# Revit family: Cadet
name_source: partatom
category: Lighting Fixtures
revit_build: Autodesk Revit Architecture 2012 (Build: 20110309_2315(x64)
units: mm (PartAtom-declared; Revit-internal decimal feet)

## types (12) — shared parameters
Apparent Load = 0 VA
Default Elevation = 48 "
Description = Cadet LED Floodlight
Glass = Hubbell - Glass
Lamp = LED
Manufacturer = Hubbell Outdoor Lighting
Manufacturer Fax = 941-751-5535
Model = Cadet
Pivot Angle = 45.00°
Visor Option = CDT : HV
Voltage = 120-277V
zz Angle 1 = 45.00°

## per-type parameters (varying)
| type | Photometric Web | Product Documentation Link | Product Material | Product Page URL | URL | Watt |
| Basic Black Textured | Web : CDT-24NB-55-3K-2X2 | http://www.beaconproducts.com | Paint - Hubbell - Basic Black Textured | http://www.beaconproducts.com | http://www.beaconproducts.com | 55 W |
| Gray Smooth | Web : CDT-24NB-55-3K-2X2 | http://www.hubbelloutdoor.com | Paint - Hubbell - Gray Smooth | http://www.hubbelloutdoor.com | http://www.hubbelloutdoor.com | 30 W |
| Black Matte Textured | Web : CDT-24NB-55-3K-2X2 | http://www.hubbelloutdoor.com | Paint - Hubbell - Black Matte Textured | http://www.hubbelloutdoor.com | http://www.hubbelloutdoor.com | 30 W |
| Bronze Textured | Web : CDT-24NB-55-3K-2X2 | http://www.hubbelloutdoor.com | Paint - Hubbell - Bronze Textured | http://www.hubbelloutdoor.com | http://www.hubbelloutdoor.com | 30 W |
| Dark Bronze Textured | Web : CDT-24NB-55-3K-2X2 | http://www.hubbelloutdoor.com | Paint - Hubbell - Dark Bronze Textured | http://www.hubbelloutdoor.com | http://www.hubbelloutdoor.com | 30 W |
| Dark Platinum Smooth | Web : CDT-24NB-55-3K-2X2 | http://www.hubbelloutdoor.com | Paint - Hubbell - Dark Platinum Smooth | http://www.hubbelloutdoor.com | http://www.hubbelloutdoor.com | 30 W |
| Green Textured | Web : CDT-24NB-55-3K-2X2 | http://www.hubbelloutdoor.com | Paint - Hubbell - Green Textured | http://www.hubbelloutdoor.com | http://www.hubbelloutdoor.com | 30 W |
| Metallic Bronze Textured | Web : CDT-24NB-55-3K-2X2 | http://www.hubbelloutdoor.com | Paint - Hubbell - Metallic Bronze Textured | http://www.hubbelloutdoor.com | http://www.hubbelloutdoor.com | 30 W |
| Metallic Silver Textured | Web : CDT-24NB-55-4K-5X5 | http://www.hubbelloutdoor.com | Paint - Hubbell - Metallic Silver Textured | http://www.hubbelloutdoor.com | http://www.hubbelloutdoor.com | 30 W |
| Metallic Titanium Textured | Web : CDT-24NB-55-3K-2X2 | http://www.hubbelloutdoor.com | Paint - Hubbell - Metallic Titanium Textured | http://www.hubbelloutdoor.com | http://www.hubbelloutdoor.com | 30 W |
| Old World Iron | Web : CDT-24NB-55-3K-2X2 | http://www.hubbelloutdoor.com | Paint - Hubbell - Old World Iron | http://www.hubbelloutdoor.com | http://www.hubbelloutdoor.com | 30 W |
| White Texture | Web : CDT-24NB-55-3K-2X2 | http://www.hubbelloutdoor.com | Paint - Hubbell - White Texture | http://www.hubbelloutdoor.com | http://www.hubbelloutdoor.com | 30 W |

## geometry (parser evidence)
native form markers: Sweep x6
no freeform markers — native parametric forms only
